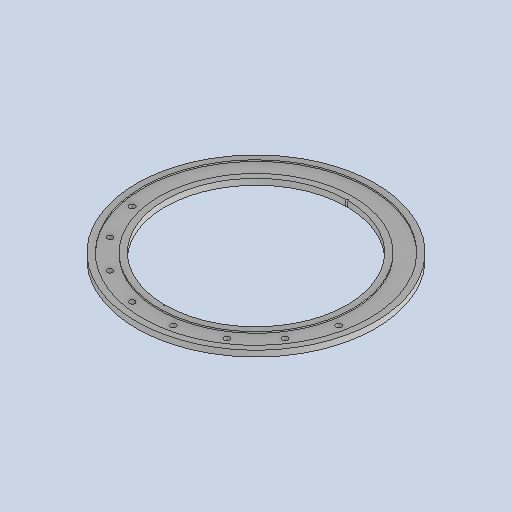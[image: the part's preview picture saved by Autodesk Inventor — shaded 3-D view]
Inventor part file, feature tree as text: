
AUTODESK INVENTOR PART (.ipt)
format: ipt  version: 2025 (Build 290162010, 162A)  size: 225,280 bytes
history: native  units: mm
features: extrude x4, sketch x4, pattern_circular x1, mirror x1, projected_geometry x1, other x1
ambient origin geometry x8: Origin, YZ Plane, XZ Plane, XY Plane, X Axis, Y Axis, Z Axis, Center Point
bodies: Solid1 (feature_tree)
feature tree (12):
  extrude  "Extrusion1"  Depth=15.0mm
  extrude  "Extrusion2"  TaperAngle=0.0deg  [1 undecoded]
  extrude  "Extrusion3"  Depth=72.0mm
  pattern_circular  "Circular Pattern2"  Count=53  [1 undecoded]
  extrude  "Extrusion4"  Depth=14.0mm
  mirror  "Mirror1"
  sketch  "Sketch1"  dims[d2=15.0mm d3=0.0mm d4=42.0mm]
  sketch  "Sketch2"  dims[d6=3.5mm d7=0.0mm d10=0.0mm d11=0.0mm]
  projected_geometry  "Projected Loop1"
  sketch  "Sketch3"  dims[d17=530.0mm d18=72.0mm d19=530.0mm]
  sketch  "Sketch5"  dims[d20=1.963495mm d21=14.0mm d22=80.0mm d23=157.5deg d34=0.0mm d35=0.0mm d40=5.0mm]
  other  "Definition1"
note: 2 required parameter values undecoded (feature->parameter linkage not recoverable at this tier; creation-order binding heuristic only, values carry confidence <= 0.55)
